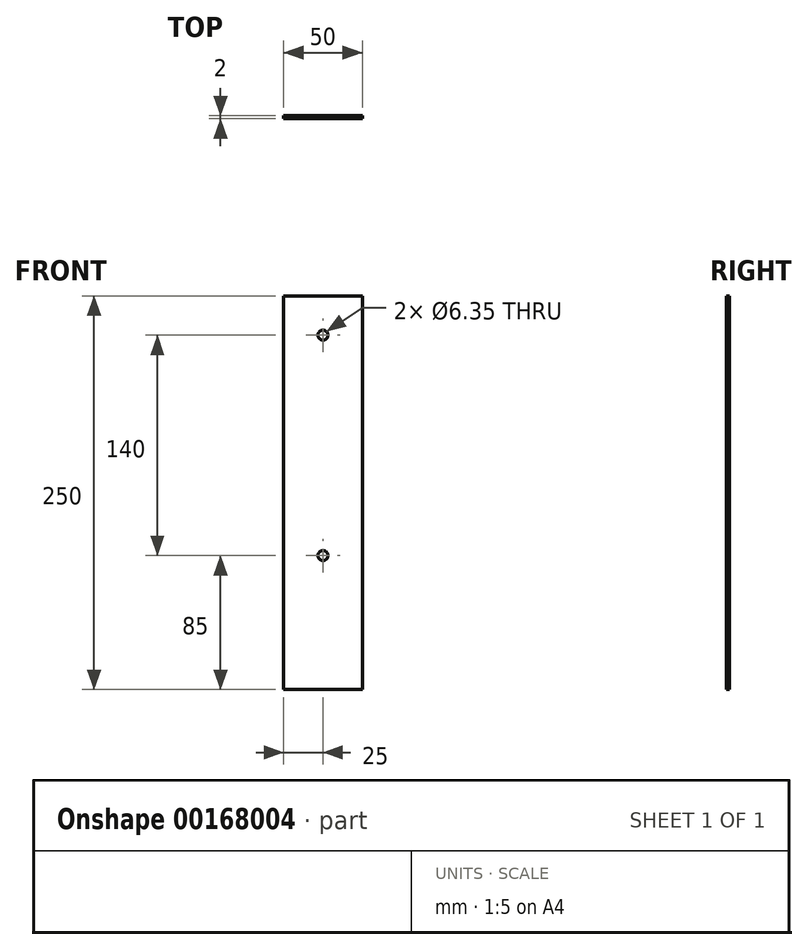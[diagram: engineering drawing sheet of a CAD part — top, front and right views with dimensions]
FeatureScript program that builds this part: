
annotation { "Feature Type Name" : "Feature", "Feature Type Description" : "" }
export const myFeature = defineFeature(function(context is Context, id is Id, definition is map)
    precondition{}
    {
        {
            var Q0;
            Q0=qCreatedBy(makeId("Front.planeOp"),FACE);
            var sketch = newSketch(context, id + "F0", { "sketchPlane" : qUnion([Q0])});
            skLineSegment(sketch, "E0.bottom", {"start": v(25, -125) * mm, "end": v(-25, -125) * mm});
            skLineSegment(sketch, "E0.top", {"start": v(25, 125) * mm, "end": v(-25, 125) * mm});
            skLineSegment(sketch, "E0.left", {"start": v(25, -125) * mm, "end": v(25, 125) * mm});
            skLineSegment(sketch, "E0.right", {"start": v(-25, -125) * mm, "end": v(-25, 125) * mm});
            skPoint(sketch, "E0.middle", {"position": v(0, 0) * mm});
            skCircle(sketch, "E1", {"center": v(0, 100) * mm, "radius": 3.18 * mm});
            skPoint(sketch, "E1.centerSnap0", {"position": v(0, 125) * mm});
            skCircle(sketch, "E2.0.7.0", {"center": v(0, -40) * mm, "radius": 3.18 * mm});
            skLineSegment(sketch, "E2.direction1", {"start": v(0, 100) * mm, "end": v(25, 100) * mm, "construction": true});
            skLineSegment(sketch, "E2.direction2", {"start": v(0, 100) * mm, "end": v(0, 80) * mm, "construction": true});
            skSolve(sketch);
        }
        {
            var Q0;
            Q0 = qSketchRegion(id + "F0", true);
            extrude(context, id + "F1", {"entities" : qUnion([Q0]), "depth" : 2 * mm, "symmetric" : true});
        }
    });
